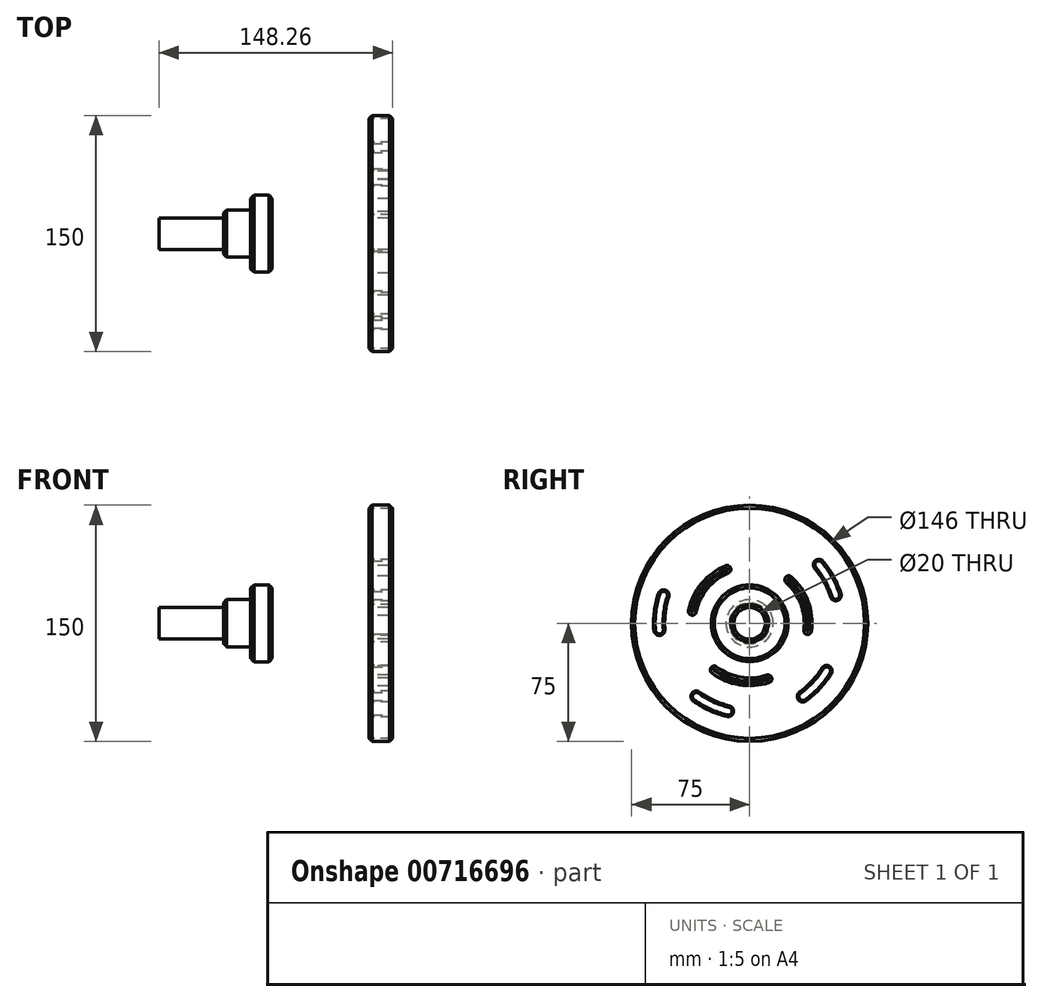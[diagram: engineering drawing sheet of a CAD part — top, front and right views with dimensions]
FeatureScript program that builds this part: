
annotation { "Feature Type Name" : "Feature", "Feature Type Description" : "" }
export const myFeature = defineFeature(function(context is Context, id is Id, definition is map)
    precondition{}
    {
        {
            var Q0;
            Q0=qCreatedBy(makeId("Right.planeOp"),FACE);
            var sketch = newSketch(context, id + "F0", { "sketchPlane" : qUnion([Q0])});
            skCircle(sketch, "E0", {"center": v(0, 0) * mm, "radius": 75 * mm});
            skCircle(sketch, "E1", {"center": v(0, 0) * mm, "radius": 10 * mm});
            skSolve(sketch);
        }
        {
            var Q0;
            Q0 = qSketchRegion(id + "F0", true);
            var Q1;
            Q1=makeQuery(id+"F0.imprint","IMPRINT",FACE,{"disambiguationData":[TD([[makeQuery(id+"F0.imprint","IMPRINT",EDGE,{"derivedFrom":sQuery(id+"F0.wireOp",EDGE,"E0")}),1.0]])]});
            extrude(context, id + "F1", {"entities" : qUnion([Q0, Q1]), "depth" : 15 * mm, "offsetDistance" : 25 * mm});
        }
        {
            var Q0;
            Q0=makeQuery(id+"F1.opExtrude","CAP_EDGE",EDGE,{"disambiguationData":[OSD([sQuery(id+"F0.wireOp",EDGE,"E0")])],"isStart":false});
            var Q1;
            Q1=makeQuery(id+"F1.opExtrude","CAP_EDGE",EDGE,{"disambiguationData":[OSD([sQuery(id+"F0.wireOp",EDGE,"E0")])],"isStart":true});
            var Q2;
            Q2=makeQuery(id+"F1.opExtrude","CAP_EDGE",EDGE,{"disambiguationData":[OSD([sQuery(id+"F0.wireOp",EDGE,"E1")])],"isStart":false});
            chamfer(context, id + "F2", {"entities" : qUnion([Q0, Q1, Q2]), "width" : 2 * mm, "tangentPropagation" : true});
        }
        {
            var Q0;
            Q0=makeQuery(id+"F1.opExtrude","CAP_FACE",FACE,{"disambiguationData":[OSD([sQuery(id+"F0.wireOp",EDGE,"E0"),sQuery(id+"F0.wireOp",EDGE,"E1")])],"isStart":false});
            var sketch = newSketch(context, id + "F3", { "sketchPlane" : qUnion([Q0])});
            skArc(sketch, "E2", {"start": v(0, 60) * mm, "mid": v(-11.56, 58.88) * mm, "end": v(-22.7, 55.54) * mm});
            skArc(sketch, "E3", {"start": v(0, 55) * mm, "mid": v(-10.6, 53.97) * mm, "end": v(-20.8, 50.91) * mm});
            skArc(sketch, "E4", {"start": v(-22.7, 55.54) * mm, "mid": v(-24.06, 52.28) * mm, "end": v(-20.8, 50.91) * mm});
            skArc(sketch, "E5", {"start": v(0, 55) * mm, "mid": v(2.5, 57.5) * mm, "end": v(0, 60) * mm});
            skArc(sketch, "E6.1.0", {"start": v(45.81, 38.75) * mm, "mid": v(42.29, 39.04) * mm, "end": v(42, 35.52) * mm});
            skArc(sketch, "E6.1.1", {"start": v(52.3, 17) * mm, "mid": v(55.46, 15.4) * mm, "end": v(57.06, 18.54) * mm});
            skArc(sketch, "E6.1.2", {"start": v(52.3, 17) * mm, "mid": v(48.05, 26.76) * mm, "end": v(42, 35.52) * mm});
            skArc(sketch, "E6.1.3", {"start": v(57.06, 18.54) * mm, "mid": v(52.42, 29.2) * mm, "end": v(45.81, 38.75) * mm});
            skArc(sketch, "E6.2.0", {"start": v(51, -31.6) * mm, "mid": v(50.2, -28.15) * mm, "end": v(46.76, -28.96) * mm});
            skArc(sketch, "E6.2.1", {"start": v(32.33, -44.5) * mm, "mid": v(31.78, -47.99) * mm, "end": v(35.27, -48.54) * mm});
            skArc(sketch, "E6.2.2", {"start": v(32.33, -44.5) * mm, "mid": v(40.3, -37.43) * mm, "end": v(46.76, -28.96) * mm});
            skArc(sketch, "E6.2.3", {"start": v(35.27, -48.54) * mm, "mid": v(43.96, -40.83) * mm, "end": v(51, -31.6) * mm});
            skArc(sketch, "E6.3.0", {"start": v(-14.29, -58.27) * mm, "mid": v(-11.27, -56.44) * mm, "end": v(-13.1, -53.42) * mm});
            skArc(sketch, "E6.3.1", {"start": v(-32.33, -44.5) * mm, "mid": v(-35.82, -45.05) * mm, "end": v(-35.27, -48.54) * mm});
            skArc(sketch, "E6.3.2", {"start": v(-32.33, -44.5) * mm, "mid": v(-23.15, -49.9) * mm, "end": v(-13.1, -53.42) * mm});
            skArc(sketch, "E6.3.3", {"start": v(-35.27, -48.54) * mm, "mid": v(-25.25, -54.43) * mm, "end": v(-14.29, -58.27) * mm});
            skArc(sketch, "E6.4.0", {"start": v(-59.84, -4.42) * mm, "mid": v(-57.16, -6.73) * mm, "end": v(-54.85, -4.05) * mm});
            skArc(sketch, "E6.4.1", {"start": v(-52.3, 17) * mm, "mid": v(-53.91, 20.15) * mm, "end": v(-57.06, 18.54) * mm});
            skArc(sketch, "E6.4.2", {"start": v(-52.3, 17) * mm, "mid": v(-54.6, 6.6) * mm, "end": v(-54.85, -4.05) * mm});
            skArc(sketch, "E6.4.3", {"start": v(-57.06, 18.54) * mm, "mid": v(-59.57, 7.2) * mm, "end": v(-59.84, -4.42) * mm});
            skLineSegment(sketch, "E6.anchor1", {"start": v(0, 0) * mm, "end": v(-20.8, 50.91) * mm, "construction": true});
            skLineSegment(sketch, "E6.anchor2", {"start": v(0, 0) * mm, "end": v(-20.8, 50.91) * mm, "construction": true});
            skSolve(sketch);
        }
        {
            var Q0;
            Q0=makeQuery(id+"F3.imprint","IMPRINT",FACE,{"disambiguationData":[TD([[makeQuery(id+"F3.imprint","IMPRINT",EDGE,{"derivedFrom":sQuery(id+"F3.wireOp",EDGE,"E4")}),1.0]])]});
            var Q1;
            Q1=makeQuery(id+"F3.imprint","IMPRINT",FACE,{"disambiguationData":[TD([[makeQuery(id+"F3.imprint","IMPRINT",EDGE,{"derivedFrom":sQuery(id+"F3.wireOp",EDGE,"E6.1.0")}),1.0]])]});
            var Q2;
            Q2=makeQuery(id+"F3.imprint","IMPRINT",FACE,{"disambiguationData":[TD([[makeQuery(id+"F3.imprint","IMPRINT",EDGE,{"derivedFrom":sQuery(id+"F3.wireOp",EDGE,"E6.2.0")}),1.0]])]});
            var Q3;
            Q3=makeQuery(id+"F3.imprint","IMPRINT",FACE,{"disambiguationData":[TD([[makeQuery(id+"F3.imprint","IMPRINT",EDGE,{"derivedFrom":sQuery(id+"F3.wireOp",EDGE,"E6.3.0")}),1.0]])]});
            var Q4;
            Q4=makeQuery(id+"F3.imprint","IMPRINT",FACE,{"disambiguationData":[TD([[makeQuery(id+"F3.imprint","IMPRINT",EDGE,{"derivedFrom":sQuery(id+"F3.wireOp",EDGE,"E6.4.0")}),1.0]])]});
            extrude(context, id + "F4", {"entities" : qUnion([Q0, Q1, Q2, Q3, Q4]), "operationType" : NewBodyOperationType.REMOVE, "endBound" : BoundingType.THROUGH_ALL, "oppositeDirection" : true, "depth" : 25 * mm, "offsetDistance" : 25 * mm});
        }
        {
            var Q0;
            Q0=makeQuery(id+"F4.boolean.opBoolean","COPY",EDGE,{"derivedFrom":makeQuery(id+"F4.opExtrude","CAP_EDGE",EDGE,{"disambiguationData":[OSD([sQuery(id+"F3.wireOp",EDGE,"E3")])],"isStart":true})});
            var Q1;
            Q1=makeQuery(id+"F4.boolean.opBoolean","COPY",EDGE,{"derivedFrom":makeQuery(id+"F4.opExtrude","CAP_EDGE",EDGE,{"disambiguationData":[OSD([sQuery(id+"F3.wireOp",EDGE,"E6.4.2")])],"isStart":true})});
            var Q2;
            Q2=makeQuery(id+"F4.boolean.opBoolean","COPY",EDGE,{"derivedFrom":makeQuery(id+"F4.opExtrude","CAP_EDGE",EDGE,{"disambiguationData":[OSD([sQuery(id+"F3.wireOp",EDGE,"E6.1.2")])],"isStart":true})});
            var Q3;
            Q3=makeQuery(id+"F4.boolean.opBoolean","COPY",EDGE,{"derivedFrom":makeQuery(id+"F4.opExtrude","CAP_EDGE",EDGE,{"disambiguationData":[OSD([sQuery(id+"F3.wireOp",EDGE,"E6.2.2")])],"isStart":true})});
            var Q4;
            Q4=makeQuery(id+"F4.boolean.opBoolean","COPY",EDGE,{"derivedFrom":makeQuery(id+"F4.opExtrude","CAP_EDGE",EDGE,{"disambiguationData":[OSD([sQuery(id+"F3.wireOp",EDGE,"E6.3.2")])],"isStart":true})});
            var Q5;
            Q5=makeQuery(id+"F4.boolean.opBoolean","INTERSECT",EDGE,{"derivedFrom":[makeQuery(id+"F1.opExtrude","CAP_FACE",FACE,{"disambiguationData":[OSD([sQuery(id+"F0.wireOp",EDGE,"E0"),sQuery(id+"F0.wireOp",EDGE,"E1")])],"isStart":true}),makeQuery(id+"F4.opExtrude","SWEPT_FACE",FACE,{"disambiguationData":[OSD([sQuery(id+"F3.wireOp",EDGE,"E3")])]})]});
            var Q6;
            Q6=makeQuery(id+"F4.boolean.opBoolean","INTERSECT",EDGE,{"derivedFrom":[makeQuery(id+"F1.opExtrude","CAP_FACE",FACE,{"disambiguationData":[OSD([sQuery(id+"F0.wireOp",EDGE,"E0"),sQuery(id+"F0.wireOp",EDGE,"E1")])],"isStart":true}),makeQuery(id+"F4.opExtrude","SWEPT_FACE",FACE,{"disambiguationData":[OSD([sQuery(id+"F3.wireOp",EDGE,"E6.4.2")])]})]});
            var Q7;
            Q7=makeQuery(id+"F4.boolean.opBoolean","INTERSECT",EDGE,{"derivedFrom":[makeQuery(id+"F1.opExtrude","CAP_FACE",FACE,{"disambiguationData":[OSD([sQuery(id+"F0.wireOp",EDGE,"E0"),sQuery(id+"F0.wireOp",EDGE,"E1")])],"isStart":true}),makeQuery(id+"F4.opExtrude","SWEPT_FACE",FACE,{"disambiguationData":[OSD([sQuery(id+"F3.wireOp",EDGE,"E6.3.2")])]})]});
            var Q8;
            Q8=makeQuery(id+"F4.boolean.opBoolean","INTERSECT",EDGE,{"derivedFrom":[makeQuery(id+"F1.opExtrude","CAP_FACE",FACE,{"disambiguationData":[OSD([sQuery(id+"F0.wireOp",EDGE,"E0"),sQuery(id+"F0.wireOp",EDGE,"E1")])],"isStart":true}),makeQuery(id+"F4.opExtrude","SWEPT_FACE",FACE,{"disambiguationData":[OSD([sQuery(id+"F3.wireOp",EDGE,"E6.2.2")])]})]});
            var Q9;
            Q9=makeQuery(id+"F4.boolean.opBoolean","INTERSECT",EDGE,{"derivedFrom":[makeQuery(id+"F1.opExtrude","CAP_FACE",FACE,{"disambiguationData":[OSD([sQuery(id+"F0.wireOp",EDGE,"E0"),sQuery(id+"F0.wireOp",EDGE,"E1")])],"isStart":true}),makeQuery(id+"F4.opExtrude","SWEPT_FACE",FACE,{"disambiguationData":[OSD([sQuery(id+"F3.wireOp",EDGE,"E6.1.2")])]})]});
            chamfer(context, id + "F5", {"entities" : qUnion([Q0, Q1, Q2, Q3, Q4, Q5, Q6, Q7, Q8, Q9]), "width" : 1 * mm, "tangentPropagation" : true});
        }
        {
            var Q0;
            Q0=makeQuery(id+"F1.opExtrude","CAP_EDGE",EDGE,{"disambiguationData":[OSD([sQuery(id+"F0.wireOp",EDGE,"E1")])],"isStart":true});
            chamfer(context, id + "F6", {"entities" : qUnion([Q0]), "width" : 2 * mm, "tangentPropagation" : true});
        }
        {
            var Q0;
            Q0=makeQuery(id+"F1.opExtrude","CAP_FACE",FACE,{"disambiguationData":[OSD([sQuery(id+"F0.wireOp",EDGE,"E0"),sQuery(id+"F0.wireOp",EDGE,"E1")])],"isStart":true});
            var sketch = newSketch(context, id + "F7", { "sketchPlane" : qUnion([Q0])});
            skArc(sketch, "E7", {"start": v(36.4, 7.6) * mm, "mid": v(28.7, 23.63) * mm, "end": v(14.43, 34.26) * mm});
            skArc(sketch, "E8.0.startCap", {"start": v(38.84, 8.1) * mm, "mid": v(36.9, 5.14) * mm, "end": v(33.94, 7.08) * mm});
            skArc(sketch, "E8.0.endCap", {"start": v(13.46, 31.95) * mm, "mid": v(12.13, 35.23) * mm, "end": v(15.4, 36.56) * mm});
            skArc(sketch, "E8.0.left", {"start": v(33.94, 7.08) * mm, "mid": v(26.77, 22.04) * mm, "end": v(13.46, 31.95) * mm});
            skArc(sketch, "E8.0.right", {"start": v(38.84, 8.1) * mm, "mid": v(30.63, 25.22) * mm, "end": v(15.4, 36.56) * mm});
            skArc(sketch, "E9.1.0", {"start": v(-26.43, 29.58) * mm, "mid": v(-22.9, 29.39) * mm, "end": v(-23.1, 25.86) * mm});
            skArc(sketch, "E9.1.1", {"start": v(-34.4, -4.32) * mm, "mid": v(-36.57, -7.1) * mm, "end": v(-39.37, -4.94) * mm});
            skArc(sketch, "E9.1.2", {"start": v(-23.1, 25.86) * mm, "mid": v(-32.47, 12.16) * mm, "end": v(-34.4, -4.32) * mm});
            skArc(sketch, "E9.1.3", {"start": v(-24.77, 27.72) * mm, "mid": v(-34.81, 13.04) * mm, "end": v(-36.88, -4.63) * mm});
            skArc(sketch, "E9.1.4", {"start": v(-26.43, 29.58) * mm, "mid": v(-37.15, 13.92) * mm, "end": v(-39.37, -4.94) * mm});
            skArc(sketch, "E9.2.0", {"start": v(-12.4, -37.69) * mm, "mid": v(-14, -34.53) * mm, "end": v(-10.84, -32.94) * mm});
            skArc(sketch, "E9.2.1", {"start": v(20.94, -27.64) * mm, "mid": v(24.44, -28.12) * mm, "end": v(23.96, -31.62) * mm});
            skArc(sketch, "E9.2.2", {"start": v(-10.84, -32.94) * mm, "mid": v(5.7, -34.2) * mm, "end": v(20.94, -27.64) * mm});
            skArc(sketch, "E9.2.3", {"start": v(-11.62, -35.31) * mm, "mid": v(6.11, -36.67) * mm, "end": v(22.45, -29.63) * mm});
            skArc(sketch, "E9.2.4", {"start": v(-12.4, -37.69) * mm, "mid": v(6.53, -39.13) * mm, "end": v(23.96, -31.62) * mm});
            skSolve(sketch);
        }
        {
            var Q0;
            Q0=makeQuery(id+"F7.imprint","IMPRINT",FACE,{"disambiguationData":[TD([[makeQuery(id+"F7.imprint","IMPRINT",EDGE,{"derivedFrom":sQuery(id+"F7.wireOp",EDGE,"E8.0.startCap")}),-1.0]])]});
            var Q1;
            Q1=makeQuery(id+"F7.imprint","IMPRINT",FACE,{"disambiguationData":[TD([[makeQuery(id+"F7.imprint","IMPRINT",EDGE,{"derivedFrom":sQuery(id+"F7.wireOp",EDGE,"E9.2.0")}),-1.0]])]});
            var Q2;
            Q2=makeQuery(id+"F7.imprint","IMPRINT",FACE,{"disambiguationData":[TD([[makeQuery(id+"F7.imprint","IMPRINT",EDGE,{"derivedFrom":sQuery(id+"F7.wireOp",EDGE,"E9.1.0")}),-1.0]])]});
            extrude(context, id + "F8", {"entities" : qUnion([Q0, Q1, Q2]), "operationType" : NewBodyOperationType.REMOVE, "endBound" : BoundingType.THROUGH_ALL, "oppositeDirection" : true, "depth" : 25 * mm, "offsetDistance" : 25 * mm});
        }
        {
            var Q0;
            Q0=makeQuery(id+"F8.boolean.opBoolean","INTERSECT",EDGE,{"derivedFrom":[makeQuery(id+"F1.opExtrude","CAP_FACE",FACE,{"disambiguationData":[OSD([sQuery(id+"F0.wireOp",EDGE,"E0"),sQuery(id+"F0.wireOp",EDGE,"E1")])],"isStart":false}),makeQuery(id+"F8.opExtrude","SWEPT_FACE",FACE,{"disambiguationData":[OSD([sQuery(id+"F7.wireOp",EDGE,"E8.0.left")])]})]});
            var Q1;
            {var subQ0=sQuery(id+"F3.wireOp",EDGE,"E3");Q1=makeQuery(id+"F5.opChamfer","BLEND_EDGE",EDGE,{"blendedFrom":[makeQuery(id+"F4.boolean.opBoolean","COPY",EDGE,{"derivedFrom":makeQuery(id+"F4.opExtrude","CAP_EDGE",EDGE,{"disambiguationData":[OSD([subQ0])],"isStart":true})}),makeQuery(id+"F4.boolean.opBoolean","COPY",FACE,{"derivedFrom":makeQuery(id+"F4.opExtrude","SWEPT_FACE",FACE,{"disambiguationData":[OSD([subQ0])]})})],"blendedInto":[makeQuery(id+"F4.boolean.opBoolean","COPY",FACE,{"derivedFrom":makeQuery(id+"F4.opExtrude","SWEPT_FACE",FACE,{"disambiguationData":[OSD([subQ0])]})})]});}
            var Q2;
            Q2=makeQuery(id+"F8.boolean.opBoolean","INTERSECT",EDGE,{"derivedFrom":[makeQuery(id+"F1.opExtrude","CAP_FACE",FACE,{"disambiguationData":[OSD([sQuery(id+"F0.wireOp",EDGE,"E0"),sQuery(id+"F0.wireOp",EDGE,"E1")])],"isStart":false}),makeQuery(id+"F8.opExtrude","SWEPT_FACE",FACE,{"disambiguationData":[OSD([sQuery(id+"F7.wireOp",EDGE,"E9.1.2")])]})]});
            var Q3;
            Q3=makeQuery(id+"F8.boolean.opBoolean","COPY",EDGE,{"derivedFrom":makeQuery(id+"F8.opExtrude","CAP_EDGE",EDGE,{"disambiguationData":[OSD([sQuery(id+"F7.wireOp",EDGE,"E9.2.2")])],"isStart":true})});
            var Q4;
            Q4=makeQuery(id+"F8.boolean.opBoolean","INTERSECT",EDGE,{"derivedFrom":[makeQuery(id+"F1.opExtrude","CAP_FACE",FACE,{"disambiguationData":[OSD([sQuery(id+"F0.wireOp",EDGE,"E0"),sQuery(id+"F0.wireOp",EDGE,"E1")])],"isStart":false}),makeQuery(id+"F8.opExtrude","SWEPT_FACE",FACE,{"disambiguationData":[OSD([sQuery(id+"F7.wireOp",EDGE,"E9.2.2")])]})]});
            chamfer(context, id + "F9", {"entities" : qUnion([Q0, Q1, Q2, Q3, Q4]), "width" : 2 * mm, "tangentPropagation" : true});
        }
        {
            var Q0;
            Q0=qCreatedBy(makeId("Front.planeOp"),FACE);
            var sketch = newSketch(context, id + "F10", { "sketchPlane" : qUnion([Q0])});
            skLineSegment(sketch, "E10", {"start": v(0, 0) * mm, "end": v(-164.24, 0) * mm, "construction": true});
            skLineSegment(sketch, "E11", {"start": v(-92.35, 10) * mm, "end": v(-92.35, 15) * mm});
            skLineSegment(sketch, "E12", {"start": v(-92.35, 15) * mm, "end": v(-75.08, 15) * mm});
            skLineSegment(sketch, "E13", {"start": v(-75.08, 15) * mm, "end": v(-75.08, 24.4) * mm});
            skLineSegment(sketch, "E14", {"start": v(-75.08, 24.4) * mm, "end": v(-61.44, 24.4) * mm});
            skLineSegment(sketch, "E15", {"start": v(-61.44, 24.4) * mm, "end": v(-61.44, 0) * mm});
            skLineSegment(sketch, "E16", {"start": v(-61.44, 0) * mm, "end": v(-133.26, 0) * mm});
            skLineSegment(sketch, "E17", {"start": v(-92.35, 10) * mm, "end": v(-133.26, 10) * mm});
            skLineSegment(sketch, "E18", {"start": v(-133.26, 10) * mm, "end": v(-133.26, 5) * mm});
            skPoint(sketch, "E19.orphan", {"position": v(-92.35, 5) * mm});
            skLineSegment(sketch, "E20", {"start": v(-133.26, 5) * mm, "end": v(-133.26, 0) * mm});
            skSolve(sketch);
        }
        {
            var Q0;
            Q0 = qSketchRegion(id + "F10", true);
            var Q1;
            Q1=sQuery(id+"F10.wireOp",EDGE,"E10");
            revolve(context, id + "F11", {"surfaceOperationType" : NewSurfaceOperationType.NEW, "entities" : qUnion([Q0]), "axis" : qUnion([Q1]), "revolveType" : RevolveType.FULL});
        }
        {
            var Q0;
            Q0=makeQuery(id+"F11.opRevolve","SWEPT_EDGE",EDGE,{"disambiguationData":[OSD([sQuery(id+"F10.wireOp",EDGE,"rklLliCn-DoYs-Keuj-d60c-ohIL3uEynHZi"),sQuery(id+"F10.wireOp",EDGE,"eSIXpwb2-XIKV-6OAx-181X-stTlBLxow6VR")])]});
            var Q1;
            Q1=makeQuery(id+"F11.opRevolve","SWEPT_EDGE",EDGE,{"disambiguationData":[OSD([sQuery(id+"F10.wireOp",EDGE,"E11"),sQuery(id+"F10.wireOp",EDGE,"E12")])]});
            var Q2;
            Q2=makeQuery(id+"F11.opRevolve","SWEPT_EDGE",EDGE,{"disambiguationData":[OSD([sQuery(id+"F10.wireOp",EDGE,"E13"),sQuery(id+"F10.wireOp",EDGE,"E14")])]});
            var Q3;
            Q3=makeQuery(id+"F11.opRevolve","SWEPT_EDGE",EDGE,{"disambiguationData":[OSD([sQuery(id+"F10.wireOp",EDGE,"E14"),sQuery(id+"F10.wireOp",EDGE,"E15")])]});
            chamfer(context, id + "F12", {"entities" : qUnion([Q0, Q1, Q2, Q3]), "width" : 2 * mm, "tangentPropagation" : true});
        }
    });
